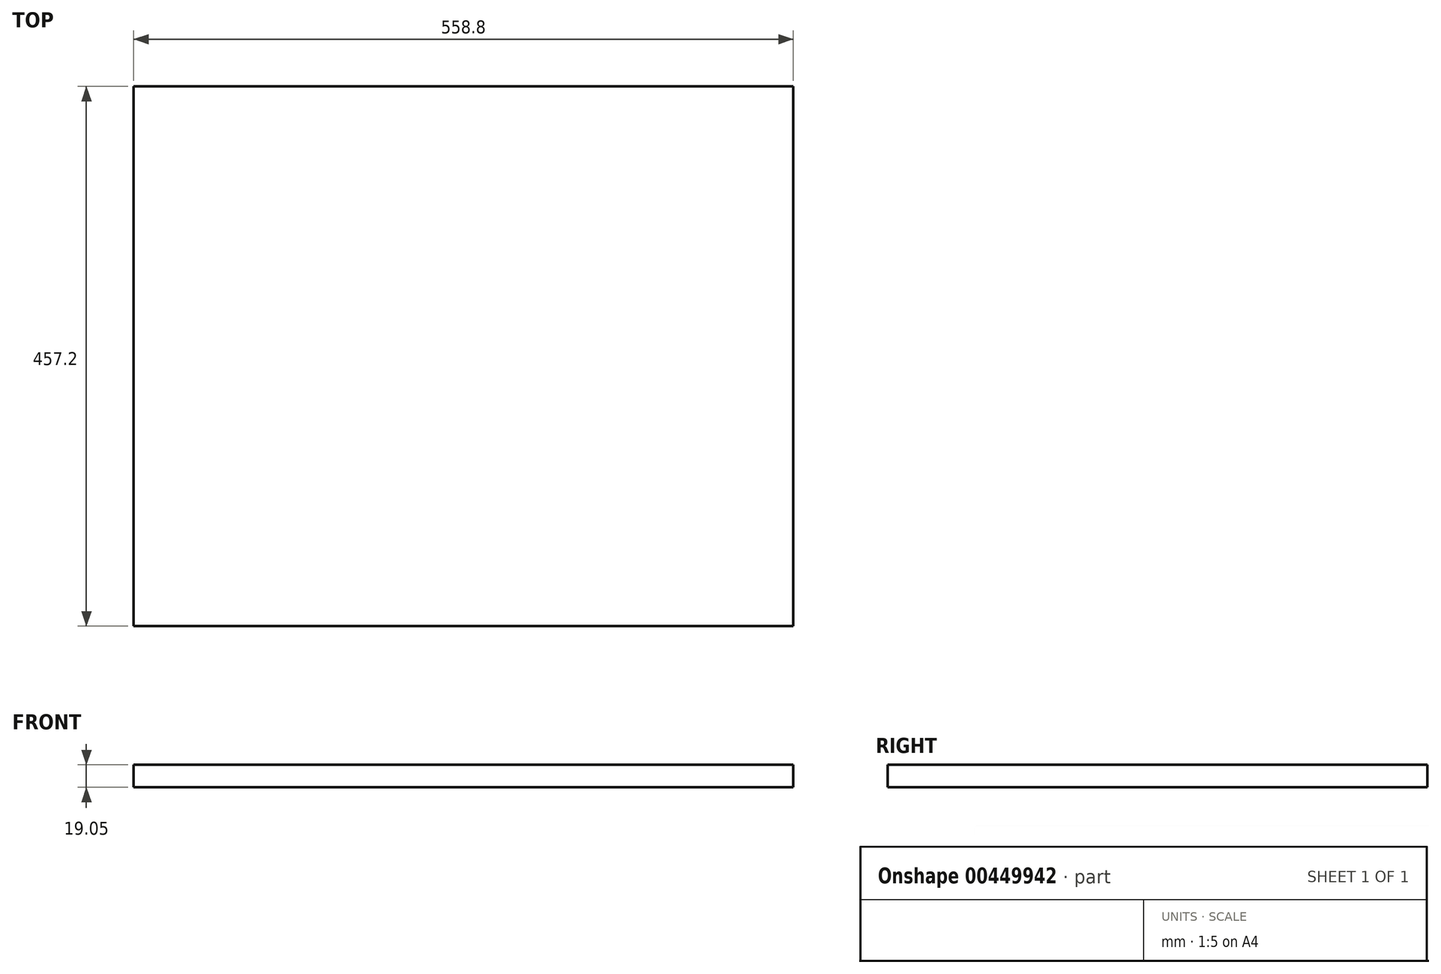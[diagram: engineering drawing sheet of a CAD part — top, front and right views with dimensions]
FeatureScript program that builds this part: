
annotation { "Feature Type Name" : "Feature", "Feature Type Description" : "" }
export const myFeature = defineFeature(function(context is Context, id is Id, definition is map)
    precondition{}
    {
        {
            var Q0;
            Q0=qCreatedBy(makeId("Top.planeOp"),FACE);
            var sketch = newSketch(context, id + "F0", { "sketchPlane" : qUnion([Q0])});
            skLineSegment(sketch, "E0.bottom", {"start": v(279.4, 228.6) * mm, "end": v(-279.4, 228.6) * mm});
            skLineSegment(sketch, "E0.top", {"start": v(279.4, -228.6) * mm, "end": v(-279.4, -228.6) * mm});
            skLineSegment(sketch, "E0.left", {"start": v(279.4, 228.6) * mm, "end": v(279.4, -228.6) * mm});
            skLineSegment(sketch, "E0.right", {"start": v(-279.4, 228.6) * mm, "end": v(-279.4, -228.6) * mm});
            skPoint(sketch, "E0.middle", {"position": v(0, 0) * mm});
            skSolve(sketch);
        }
        {
            var Q0;
            Q0 = qSketchRegion(id + "F0", true);
            extrude(context, id + "F1", {"entities" : qUnion([Q0]), "depth" : 19.05 * mm});
        }
    });
